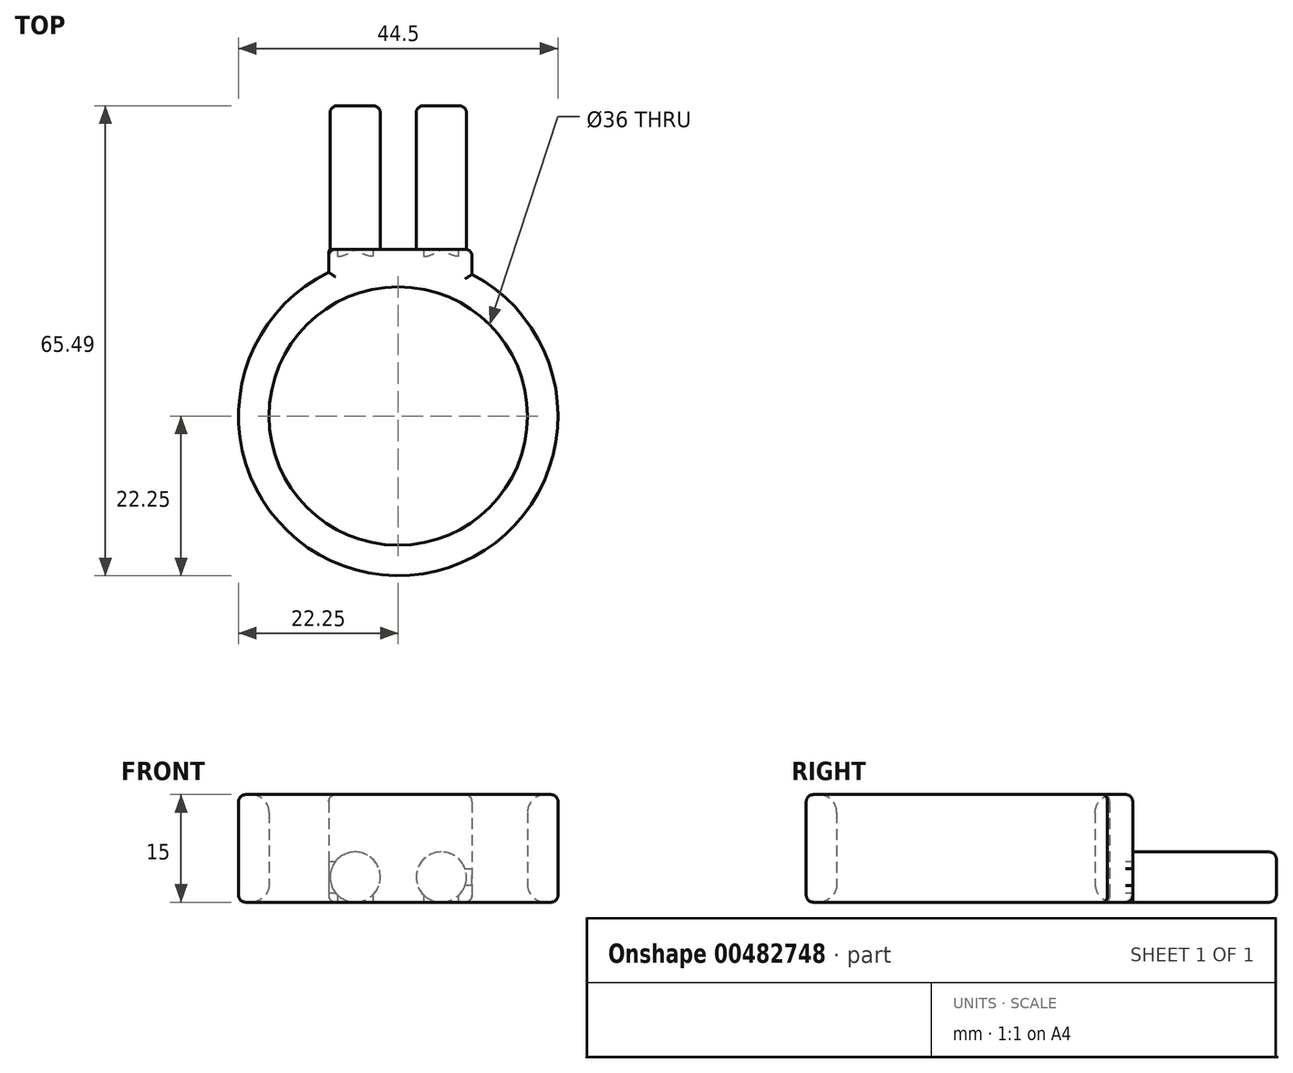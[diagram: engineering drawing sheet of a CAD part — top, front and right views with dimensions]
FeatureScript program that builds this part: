
annotation { "Feature Type Name" : "Feature", "Feature Type Description" : "" }
export const myFeature = defineFeature(function(context is Context, id is Id, definition is map)
    precondition{}
    {
        {
            var Q0;
            Q0=qCreatedBy(makeId("Top.planeOp"),FACE);
            var sketch = newSketch(context, id + "F0", { "sketchPlane" : qUnion([Q0])});
            skArc(sketch, "E0", {"start": v(-9.71, 20.02) * mm, "mid": v(-0.32, -22.25) * mm, "end": v(10.29, 19.73) * mm});
            skCircle(sketch, "E1", {"center": v(0, 0) * mm, "radius": 18 * mm});
            skLineSegment(sketch, "E2.top", {"start": v(-9.71, 23.24) * mm, "end": v(10.29, 23.24) * mm});
            skLineSegment(sketch, "E2.left", {"start": v(-9.71, 20.02) * mm, "end": v(-9.71, 23.24) * mm});
            skLineSegment(sketch, "E2.right", {"start": v(10.29, 19.73) * mm, "end": v(10.29, 23.24) * mm});
            skSolve(sketch);
        }
        {
            var Q0;
            Q0=makeQuery(id+"F0.imprint","IMPRINT",FACE,{"disambiguationData":[TD([[makeQuery(id+"F0.imprint","IMPRINT",EDGE,{"derivedFrom":sQuery(id+"F0.wireOp",EDGE,"E0")}),1.0]])]});
            extrude(context, id + "F1", {"entities" : qUnion([Q0]), "depth" : 15 * mm});
        }
        {
            var Q0;
            Q0=makeQuery(id+"F1.opExtrude","SWEPT_FACE",FACE,{"disambiguationData":[OSD([sQuery(id+"F0.wireOp",EDGE,"E2.top")])]});
            cPlane(context, id + "F2", {"entities" : qUnion([Q0]), "cplaneType" : CPlaneType.OFFSET, "offset" : 0 * mm, "width" : 150 * mm, "height" : 150 * mm});
        }
        {
            var Q0;
            Q0=qCreatedBy(id+"F2.planeOp",FACE);
            var sketch = newSketch(context, id + "F3", { "sketchPlane" : qUnion([Q0])});
            skCircle(sketch, "E3", {"center": v(-6, 3.5) * mm, "radius": 3.5 * mm});
            skCircle(sketch, "E4", {"center": v(6, 3.5) * mm, "radius": 3.5 * mm});
            skSolve(sketch);
        }
        {
            var Q0;
            Q0=makeQuery(id+"F3.imprint","IMPRINT",FACE,{"disambiguationData":[TD([[makeQuery(id+"F3.imprint","IMPRINT",EDGE,{"derivedFrom":sQuery(id+"F3.wireOp",EDGE,"E3")}),1.0]])]});
            var Q1;
            Q1=makeQuery(id+"F3.imprint","IMPRINT",FACE,{"disambiguationData":[TD([[makeQuery(id+"F3.imprint","IMPRINT",EDGE,{"derivedFrom":sQuery(id+"F3.wireOp",EDGE,"E4")}),1.0]])]});
            extrude(context, id + "F4", {"entities" : qUnion([Q0, Q1]), "operationType" : NewBodyOperationType.ADD, "depth" : 20 * mm, "hasSecondDirection" : true, "secondDirectionOppositeDirection" : true, "secondDirectionDepth" : 3 * mm});
        }
        {
            var Q0;
            Q0=makeQuery(id+"F1.opExtrude","CAP_EDGE",EDGE,{"disambiguationData":[OSD([sQuery(id+"F0.wireOp",EDGE,"E0")])],"isStart":true});
            var Q1;
            Q1=makeQuery(id+"F1.opExtrude","CAP_EDGE",EDGE,{"disambiguationData":[OSD([sQuery(id+"F0.wireOp",EDGE,"E0")])],"isStart":false});
            var Q2;
            Q2=makeQuery(id+"F1.opExtrude","SWEPT_EDGE",EDGE,{"disambiguationData":[OSD([sQuery(id+"F0.wireOp",EDGE,"E2.top"),sQuery(id+"F0.wireOp",EDGE,"E2.left")])]});
            var Q3;
            Q3=makeQuery(id+"F1.opExtrude","CAP_EDGE",EDGE,{"disambiguationData":[OSD([sQuery(id+"F0.wireOp",EDGE,"E2.top")])],"isStart":false});
            var Q4;
            Q4=makeQuery(id+"F1.opExtrude","SWEPT_EDGE",EDGE,{"disambiguationData":[OSD([sQuery(id+"F0.wireOp",EDGE,"E2.top"),sQuery(id+"F0.wireOp",EDGE,"E2.right")])]});
            var Q5;
            Q5=makeQuery(id+"F1.opExtrude","CAP_EDGE",EDGE,{"disambiguationData":[OSD([sQuery(id+"F0.wireOp",EDGE,"E2.top")])],"isStart":true});
            var Q6;
            Q6=makeQuery(id+"F1.opExtrude","CAP_EDGE",EDGE,{"disambiguationData":[OSD([sQuery(id+"F0.wireOp",EDGE,"E2.left")])],"isStart":true});
            var Q7;
            Q7=makeQuery(id+"F1.opExtrude","CAP_EDGE",EDGE,{"disambiguationData":[OSD([sQuery(id+"F0.wireOp",EDGE,"E2.left")])],"isStart":false});
            var Q8;
            Q8=makeQuery(id+"F1.opExtrude","CAP_EDGE",EDGE,{"disambiguationData":[OSD([sQuery(id+"F0.wireOp",EDGE,"E2.right")])],"isStart":false});
            var Q9;
            Q9=makeQuery(id+"F1.opExtrude","CAP_EDGE",EDGE,{"disambiguationData":[OSD([sQuery(id+"F0.wireOp",EDGE,"E2.right")])],"isStart":true});
            var Q10;
            Q10=makeQuery(id+"F4.opExtrude","CAP_EDGE",EDGE,{"disambiguationData":[OSD([sQuery(id+"F3.wireOp",EDGE,"E3")])],"isStart":false});
            var Q11;
            Q11=makeQuery(id+"F4.opExtrude","CAP_EDGE",EDGE,{"disambiguationData":[OSD([sQuery(id+"F3.wireOp",EDGE,"E4")])],"isStart":false});
            fillet(context, id + "F5", {"entities" : qUnion([Q0, Q1, Q2, Q3, Q4, Q5, Q6, Q7, Q8, Q9, Q10, Q11]), "radius" : 1 * mm, "tangentPropagation" : true, "allowEdgeOverflow" : false});
        }
        {
            var Q0;
            Q0=makeQuery(id+"F3NnvlL0xeerbJF_1.splitOp","SPLIT",EDGE,{"derivedFrom":makeQuery(id+"F1.opExtrude","CAP_EDGE",EDGE,{"disambiguationData":[OSD([sQuery(id+"F0.wireOp",EDGE,"E1")])],"isStart":false}),"isFromBackBody":true});
            var Q1;
            Q1=makeQuery(id+"F3NnvlL0xeerbJF_1.splitOp","SPLIT",EDGE,{"derivedFrom":makeQuery(id+"F1.opExtrude","CAP_EDGE",EDGE,{"disambiguationData":[OSD([sQuery(id+"F0.wireOp",EDGE,"E1")])],"isStart":false})});
            var Q2;
            Q2=makeQuery(id+"F3NnvlL0xeerbJF_1.splitOp","SPLIT",EDGE,{"derivedFrom":makeQuery(id+"F1.opExtrude","CAP_EDGE",EDGE,{"disambiguationData":[OSD([sQuery(id+"F0.wireOp",EDGE,"E1")])],"isStart":true}),"isFromBackBody":true});
            var Q3;
            Q3=makeQuery(id+"F3NnvlL0xeerbJF_1.splitOp","SPLIT",EDGE,{"derivedFrom":makeQuery(id+"F1.opExtrude","CAP_EDGE",EDGE,{"disambiguationData":[OSD([sQuery(id+"F0.wireOp",EDGE,"E1")])],"isStart":true})});
            fillet(context, id + "F6", {"entities" : qUnion([Q0, Q1, Q2, Q3]), "radius" : 2.5 * mm, "tangentPropagation" : true, "allowEdgeOverflow" : false});
        }
    });
